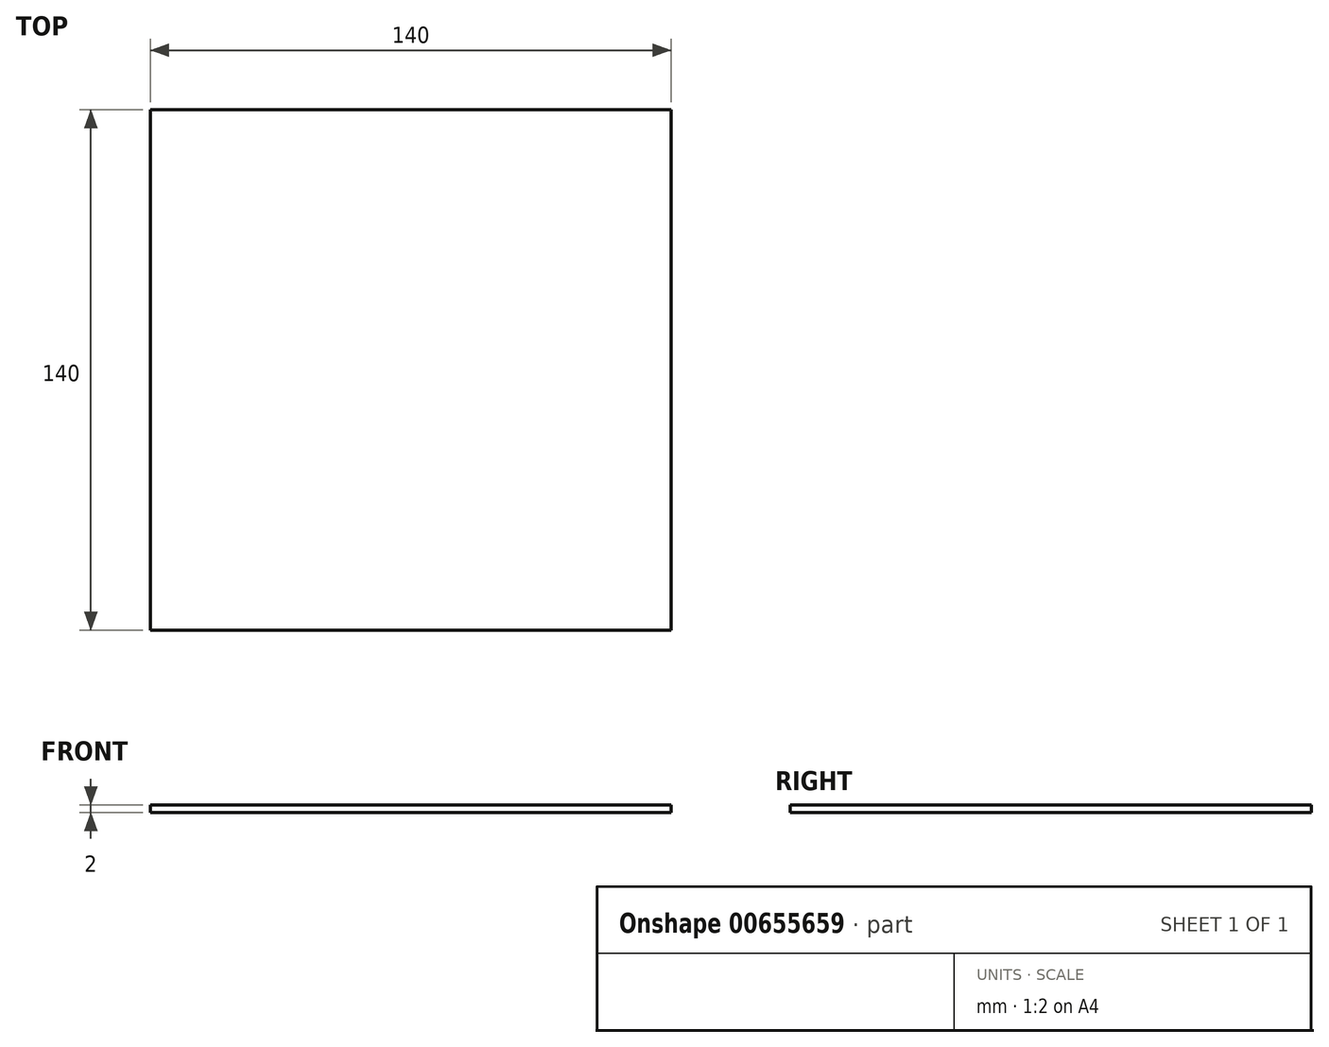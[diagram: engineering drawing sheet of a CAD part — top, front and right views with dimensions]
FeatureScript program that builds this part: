
annotation { "Feature Type Name" : "Feature", "Feature Type Description" : "" }
export const myFeature = defineFeature(function(context is Context, id is Id, definition is map)
    precondition{}
    {
        {
            var Q0;
            Q0=qCreatedBy(makeId("Top.planeOp"),FACE);
            var sketch = newSketch(context, id + "F0", { "sketchPlane" : qUnion([Q0])});
            skLineSegment(sketch, "E0.bottom", {"start": v(-70, 70) * mm, "end": v(70, 70) * mm});
            skLineSegment(sketch, "E0.top", {"start": v(-70, -70) * mm, "end": v(70, -70) * mm});
            skLineSegment(sketch, "E0.left", {"start": v(-70, 70) * mm, "end": v(-70, -70) * mm});
            skLineSegment(sketch, "E0.right", {"start": v(70, 70) * mm, "end": v(70, -70) * mm});
            skLineSegment(sketch, "E1", {"start": v(0, 70) * mm, "end": v(0, -70) * mm});
            skSolve(sketch);
        }
        {
            var Q0;
            Q0 = qSketchRegion(id + "F0", true);
            extrude(context, id + "F1", {"entities" : qUnion([Q0]), "depth" : 2 * mm, "offsetDistance" : 25 * mm});
        }
    });
